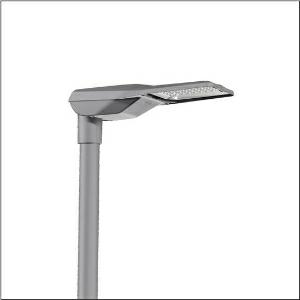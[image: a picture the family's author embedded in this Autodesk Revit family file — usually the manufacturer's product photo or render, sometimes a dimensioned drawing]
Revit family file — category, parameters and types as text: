
# Revit family: streetlight_sl_21_iq_mini___st1_0a_5xe2d21d08hb_1c5e
name_source: partatom
category: Lighting Fixtures
units: mm (PartAtom-declared; Revit-internal decimal feet)

## family parameters
Cut with Voids When Loaded = No
Host = Face
Light Source = No
Part Type = Normal
Room Calculation Point = No
Round Connector Dimension = Use Diameter
Shared = No

## types (1)
- --- (1 x LED, 7830 lm, 70.9 W, 2200K)
    Apparent Load = 71 VA
    CIE Flux Codes = 37 72 97 100 100
    Color Rendering = 70
    Color Temperature = 2200K
    Default Elevation = 1800 mm
    Description = Streetlight SL 21 iQ mini, mast luminaire, primary light control with lens, of PMMA, primary optical cover: cover, of toughened safety glass, transparent, light distribution: ST1.0a, light emission: direct distribution, primary light characteristic: asymmetric, installation type: post-top, side-entry, LED, High Power LED, rated luminous flux: 7.830lm, luminous efficacy: 110lm/W, light colour: 722, colour temperature: 2200K, control gear: iQ-Comfort, control: Auto-Match, Temp-Guard, Lumen-Switch, Night-Set, Smart-Wire, Light-Fading, Desk-Remote (wireless, voltage-free reading and setting of iQ features in the workshop via application-optimized NFC function/RFID function), optimised constant luminous flux control (CLO 2.0), pre-setting: linear dimming characteristic, mains connection: 220..240V, AC, 50/60Hz, start of lifetime: 71W, end of service life: 75W, reduction: 31W, luminaire housing, of diecast aluminium, powder-coated, SITECO metallic grey (DB 702S), corrosivity category C5 high according to DIN EN ISO 12944, please order mast flange separately, inclination adjustable: 0°, 5°, 10°, 15°, sealing non-destructively replaceable, multi-level sealing system, length: 628mm, width: 235mm, height: 110mm, mast flange for spigot size: 42mm (side-entry): 5XC10008XM4, 60/48mm (side-entry/post-top): 5XC10108XM2, 76/60mm (side-entry/post-top): 5XC10108XM1, mounting height: 4..8m, protection rating (complete): IP66, insulation class (complete): insulation class II (safety insulation), certification: CE, ENEC, ENEC+, VDE, impact resistance: IK10, permissible operating ambient temperature for outdoor applications: -40..+50°C, standard-compliant lighting for roads and squares, packaging unit: 1 piece

Light Distribution: ST1.0a
    Height = 110 mm
    Lamp = 1 x LED
    Lamp Light Flux = 7830 lm
    Lamp Power = 70.9 W
    Lamp count = 1
    Length = 625 mm
    Luminous efficacy = 110 lm/W
    Manufacturer = Siteco
    ModVariant = No
    Model = 5XE2D21D08HB
    Number of Poles = 1
    OnlyDefault = Yes
    Power Factor = 1
    Product Name = Streetlight SL 21 iQ mini | ST1.0a
    Product group = mast luminaire | pylon top
    ProductGroupID = 6100
    Protection Class = Protection class II
    Protection Degree = IP 66
    RLX_Detail_Level = 1
    RLX_Emergency_Light_Flux = 0 lm
    RLX_Emergency_Type = 0
    RLX_Emergency_Type_DB = No
    RlxData = <blob elided: 26233 chars, md5=ebdc49a6>
    Socket = socket
    Standby Power = 0 W
    System Light Flux = 7830 lm
    System Power = 71 W
    Type Comments = factory setting: luminous flux: 100 % | dim-lin: 254 | 711 mA
    Type Image = l_1003519.jpg
    URL = http://relux.com
    VarID = @adj_157793
    Voltage = 0 V
    Weight = 0.00 kg
    Width = 234 mm

## geometry (parser evidence)
native form markers: Blend x4, Sweep x11
no freeform markers — native parametric forms only
